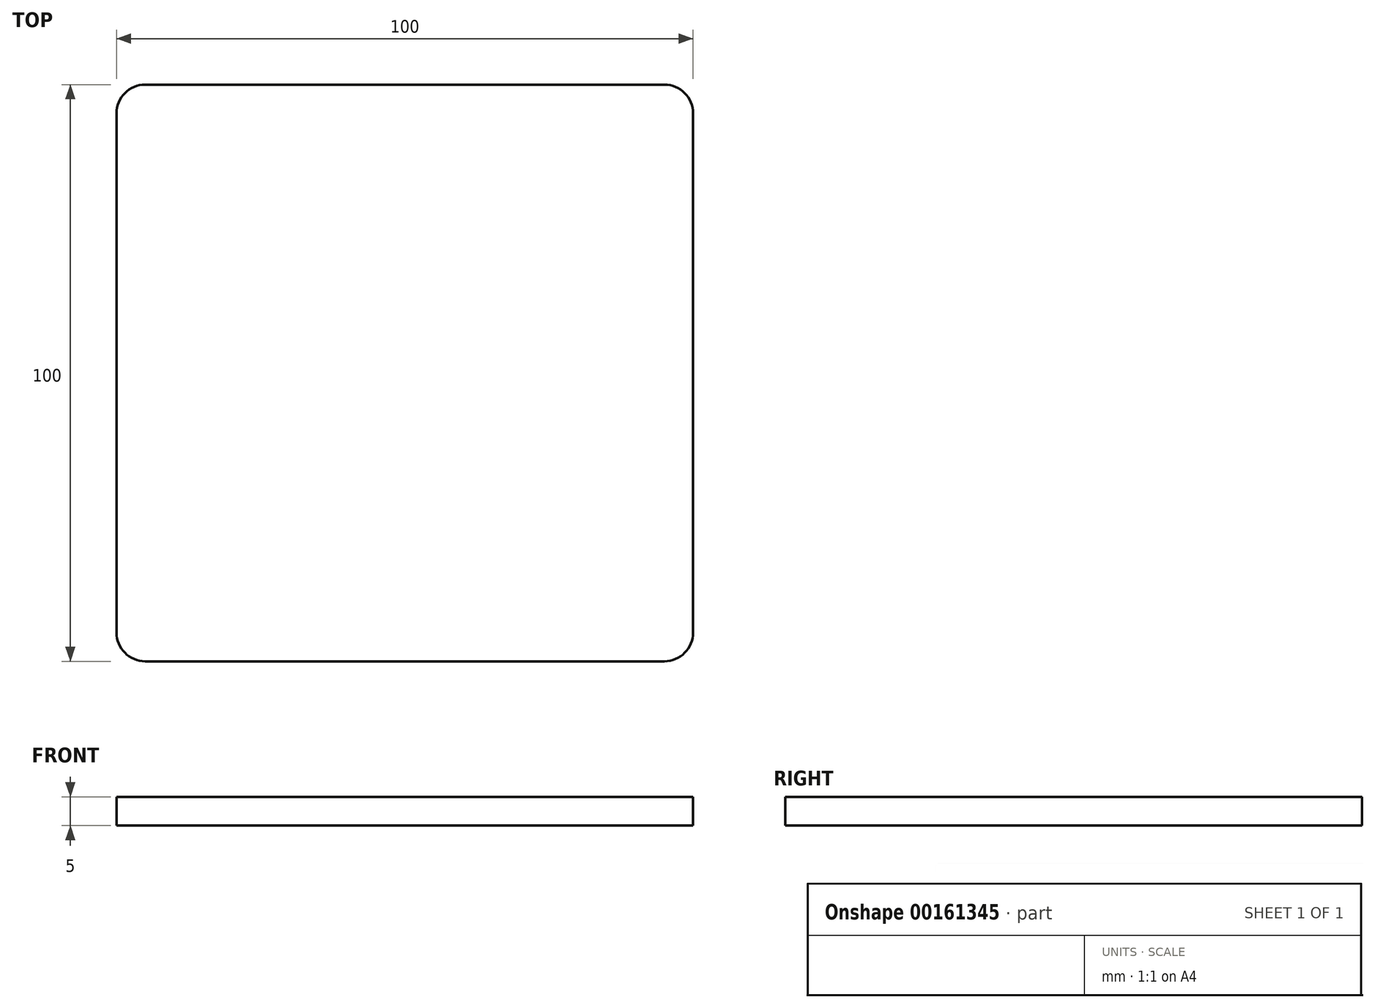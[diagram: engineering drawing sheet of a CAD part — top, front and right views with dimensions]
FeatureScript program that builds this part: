
annotation { "Feature Type Name" : "Feature", "Feature Type Description" : "" }
export const myFeature = defineFeature(function(context is Context, id is Id, definition is map)
    precondition{}
    {
        {
            var Q0;
            Q0=qCreatedBy(makeId("Top.planeOp"),FACE);
            var sketch = newSketch(context, id + "F0", { "sketchPlane" : qUnion([Q0])});
            skLineSegment(sketch, "E0.bottom", {"start": v(50, 50) * mm, "end": v(-50, 50) * mm});
            skLineSegment(sketch, "E0.top", {"start": v(50, -50) * mm, "end": v(-50, -50) * mm});
            skLineSegment(sketch, "E0.left", {"start": v(50, 50) * mm, "end": v(50, -50) * mm});
            skLineSegment(sketch, "E0.right", {"start": v(-50, 50) * mm, "end": v(-50, -50) * mm});
            skPoint(sketch, "E0.middle", {"position": v(0, 0) * mm});
            skSolve(sketch);
        }
        {
            var Q0;
            Q0=makeQuery(id+"F0.imprint","IMPRINT",FACE,{"disambiguationData":[TD([[makeQuery(id+"F0.imprint","IMPRINT",EDGE,{"derivedFrom":sQuery(id+"F0.wireOp",EDGE,"E0.bottom")}),1.0]])]});
            extrude(context, id + "F1", {"entities" : qUnion([Q0]), "oppositeDirection" : true, "depth" : 5 * mm});
        }
        {
            var Q0;
            Q0=makeQuery(id+"F1.opExtrude","SWEPT_EDGE",EDGE,{"disambiguationData":[OSD([sQuery(id+"F0.wireOp",EDGE,"E0.top"),sQuery(id+"F0.wireOp",EDGE,"E0.left")])]});
            var Q1;
            Q1=makeQuery(id+"F1.opExtrude","SWEPT_EDGE",EDGE,{"disambiguationData":[OSD([sQuery(id+"F0.wireOp",EDGE,"E0.top"),sQuery(id+"F0.wireOp",EDGE,"E0.right")])]});
            var Q2;
            Q2=makeQuery(id+"F1.opExtrude","SWEPT_EDGE",EDGE,{"disambiguationData":[OSD([sQuery(id+"F0.wireOp",EDGE,"E0.bottom"),sQuery(id+"F0.wireOp",EDGE,"E0.left")])]});
            var Q3;
            Q3=makeQuery(id+"F1.opExtrude","SWEPT_EDGE",EDGE,{"disambiguationData":[OSD([sQuery(id+"F0.wireOp",EDGE,"E0.bottom"),sQuery(id+"F0.wireOp",EDGE,"E0.right")])]});
            fillet(context, id + "F2", {"entities" : qUnion([Q0, Q1, Q2, Q3]), "radius" : 5 * mm, "tangentPropagation" : true, "allowEdgeOverflow" : false});
        }
    });
